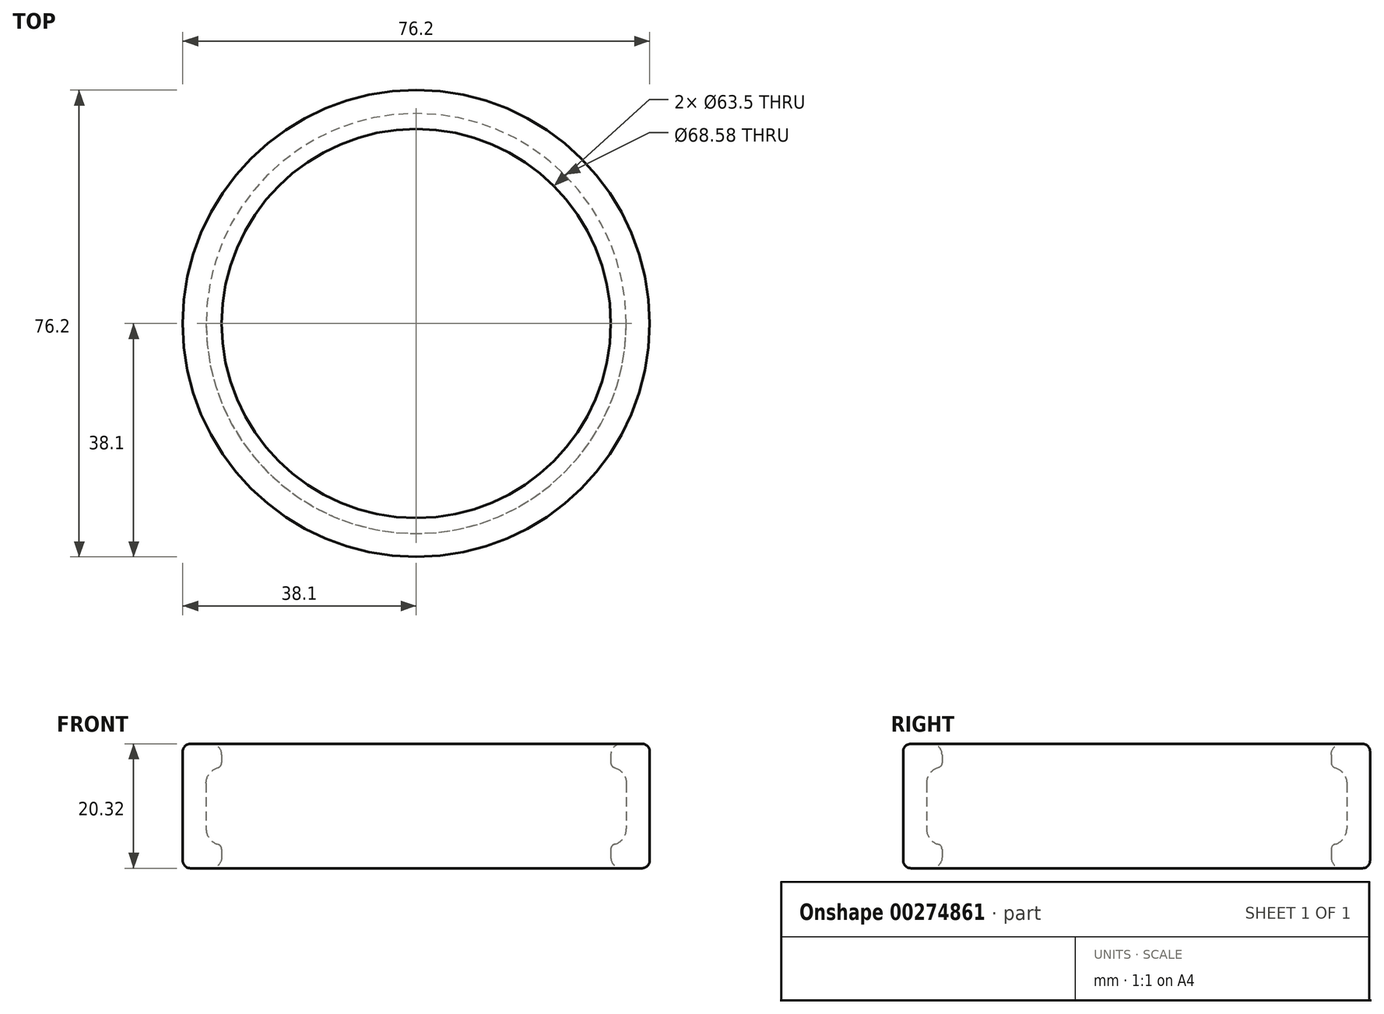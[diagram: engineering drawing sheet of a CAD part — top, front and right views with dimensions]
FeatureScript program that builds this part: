
annotation { "Feature Type Name" : "Feature", "Feature Type Description" : "" }
export const myFeature = defineFeature(function(context is Context, id is Id, definition is map)
    precondition{}
    {
        {
            var Q0;
            Q0=qCreatedBy(makeId("Top.planeOp"),FACE);
            var sketch = newSketch(context, id + "F0", { "sketchPlane" : qUnion([Q0])});
            skCircle(sketch, "E0", {"center": v(0, 0) * mm, "radius": 38.1 * mm});
            skCircle(sketch, "E1", {"center": v(0, 0) * mm, "radius": 31.75 * mm});
            skSolve(sketch);
        }
        {
            var Q0;
            Q0=makeQuery(id+"F0.imprint","IMPRINT",FACE,{"disambiguationData":[TD([[makeQuery(id+"F0.imprint","IMPRINT",EDGE,{"derivedFrom":sQuery(id+"F0.wireOp",EDGE,"E0")}),-1.0]])]});
            var Q1;
            Q1=makeQuery(id+"F0.imprint","IMPRINT",FACE,{"disambiguationData":[TD([[makeQuery(id+"F0.imprint","IMPRINT",EDGE,{"derivedFrom":sQuery(id+"F0.wireOp",EDGE,"E0")}),1.0]])]});
            extrude(context, id + "F1", {"entities" : qUnion([Q0, Q1]), "endBound" : BoundingType.SYMMETRIC, "depth" : 20.32 * mm});
        }
        {
            var Q0;
            Q0=makeQuery(id+"F1.opExtrude","SWEPT_FACE",FACE,{"disambiguationData":[OSD([sQuery(id+"F0.wireOp",EDGE,"E1")])]});
            shell(context, id + "F2", {"entities" : qUnion([Q0]), "thickness" : 3.8 * mm});
        }
        {
            var Q0;
            Q0=makeQuery(id+"F1.opExtrude","CAP_EDGE",EDGE,{"disambiguationData":[OSD([sQuery(id+"F0.wireOp",EDGE,"E1")])],"isStart":false});
            var Q1;
            Q1=makeQuery(id+"F1.opExtrude","CAP_EDGE",EDGE,{"disambiguationData":[OSD([sQuery(id+"F0.wireOp",EDGE,"E1")])],"isStart":true});
            fillet(context, id + "F3", {"entities" : qUnion([Q0, Q1]), "radius" : 1.78 * mm, "tangentPropagation" : true, "allowEdgeOverflow" : false});
        }
        {
            var Q0;
            {var subQ0=sQuery(id+"F0.wireOp",EDGE,"E0");var subQ1=sQuery(id+"F0.wireOp",EDGE,"E1");Q0=makeQuery(id+"FkAHEVNdcQpRxt2_1.opFillet","BLEND_EDGE",EDGE,{"blendedFrom":[makeQuery(id+"F50xpF200IVCPWQ_1.opThicken","CAP_EDGE",EDGE,{"disambiguationData":[OSD([subQ1]),TDD([makeQuery(id+"F2.opShell","OFFSET_EDGE",EDGE,{"disambiguationData":[OSD([subQ1]),TDD([makeQuery(id+"F1.opExtrude","CAP_EDGE",EDGE,{"disambiguationData":[OSD([subQ1])],"isStart":true})])]})])],"isStart":true}),makeQuery(id+"F50xpF200IVCPWQ_1.boolean.opBoolean","MERGE",FACE,{"derivedFrom":[makeQuery(id+"F2.opShell","OFFSET_FACE",FACE,{"disambiguationData":[OSD([subQ0])]}),makeQuery(id+"F50xpF200IVCPWQ_1.opThicken","SWEPT_FACE",FACE,{"disambiguationData":[OSD([subQ0]),TDD([makeQuery(id+"F2.opShell","OFFSET_EDGE",EDGE,{"disambiguationData":[OSD([subQ0]),TDD([makeQuery(id+"F1.opExtrude","CAP_EDGE",EDGE,{"disambiguationData":[OSD([subQ0])],"isStart":true})])]})])]})]})],"blendedInto":[makeQuery(id+"F50xpF200IVCPWQ_1.boolean.opBoolean","MERGE",FACE,{"derivedFrom":[makeQuery(id+"F2.opShell","OFFSET_FACE",FACE,{"disambiguationData":[OSD([subQ0])]}),makeQuery(id+"F50xpF200IVCPWQ_1.opThicken","SWEPT_FACE",FACE,{"disambiguationData":[OSD([subQ0]),TDD([makeQuery(id+"F2.opShell","OFFSET_EDGE",EDGE,{"disambiguationData":[OSD([subQ0]),TDD([makeQuery(id+"F1.opExtrude","CAP_EDGE",EDGE,{"disambiguationData":[OSD([subQ0])],"isStart":true})])]})])]})]})]});}
            var Q1;
            Q1=makeQuery(id+"F1.opExtrude","CAP_EDGE",EDGE,{"disambiguationData":[OSD([sQuery(id+"F0.wireOp",EDGE,"E0")])],"isStart":true});
            var Q2;
            Q2=makeQuery(id+"F1.opExtrude","CAP_EDGE",EDGE,{"disambiguationData":[OSD([sQuery(id+"F0.wireOp",EDGE,"E0")])],"isStart":false});
            var Q3;
            {var subQ0=sQuery(id+"F0.wireOp",EDGE,"E0");var subQ1=sQuery(id+"F0.wireOp",EDGE,"E1");Q3=makeQuery(id+"FkAHEVNdcQpRxt2_1.opFillet","BLEND_EDGE",EDGE,{"blendedFrom":[makeQuery(id+"F50xpF200IVCPWQ_1.opThicken","CAP_EDGE",EDGE,{"disambiguationData":[OSD([subQ1]),TDD([makeQuery(id+"F2.opShell","OFFSET_EDGE",EDGE,{"disambiguationData":[OSD([subQ1]),TDD([makeQuery(id+"F1.opExtrude","CAP_EDGE",EDGE,{"disambiguationData":[OSD([subQ1])],"isStart":false})])]})])],"isStart":true}),makeQuery(id+"F50xpF200IVCPWQ_1.boolean.opBoolean","MERGE",FACE,{"derivedFrom":[makeQuery(id+"F1.opExtrude","SWEPT_FACE",FACE,{"disambiguationData":[OSD([subQ0])]}),makeQuery(id+"F50xpF200IVCPWQ_1.opThicken","SWEPT_FACE",FACE,{"disambiguationData":[OSD([subQ0]),TDD([makeQuery(id+"F2.opShell","OFFSET_EDGE",EDGE,{"disambiguationData":[OSD([subQ0]),TDD([makeQuery(id+"F1.opExtrude","CAP_EDGE",EDGE,{"disambiguationData":[OSD([subQ0])],"isStart":false})])]})])]})]})],"blendedInto":[makeQuery(id+"F50xpF200IVCPWQ_1.boolean.opBoolean","MERGE",FACE,{"derivedFrom":[makeQuery(id+"F1.opExtrude","SWEPT_FACE",FACE,{"disambiguationData":[OSD([subQ0])]}),makeQuery(id+"F50xpF200IVCPWQ_1.opThicken","SWEPT_FACE",FACE,{"disambiguationData":[OSD([subQ0]),TDD([makeQuery(id+"F2.opShell","OFFSET_EDGE",EDGE,{"disambiguationData":[OSD([subQ0]),TDD([makeQuery(id+"F1.opExtrude","CAP_EDGE",EDGE,{"disambiguationData":[OSD([subQ0])],"isStart":false})])]})])]})]})]});}
            fillet(context, id + "F4", {"entities" : qUnion([Q0, Q1, Q2, Q3]), "radius" : 1.27 * mm, "tangentPropagation" : true, "allowEdgeOverflow" : false});
        }
        {
            var Q0;
            {var subQ0=sQuery(id+"F0.wireOp",EDGE,"E0");Q0=makeQuery(id+"F2.opShell","OFFSET_EDGE",EDGE,{"disambiguationData":[OSD([subQ0]),TDD([makeQuery(id+"F1.opExtrude","CAP_EDGE",EDGE,{"disambiguationData":[OSD([subQ0])],"isStart":true})])]});}
            var Q1;
            {var subQ0=sQuery(id+"F0.wireOp",EDGE,"E0");Q1=makeQuery(id+"F2.opShell","OFFSET_EDGE",EDGE,{"disambiguationData":[OSD([subQ0]),TDD([makeQuery(id+"F1.opExtrude","CAP_EDGE",EDGE,{"disambiguationData":[OSD([subQ0])],"isStart":false})])]});}
            fillet(context, id + "F5", {"entities" : qUnion([Q0, Q1]), "radius" : 2.64 * mm, "tangentPropagation" : true, "allowEdgeOverflow" : false});
        }
        {
            var Q0;
            {var subQ0=sQuery(id+"F0.wireOp",EDGE,"E0");Q0=makeQuery(id+"F5.opFillet","BLEND_EDGE",EDGE,{"blendedFrom":[makeQuery(id+"F2.opShell","OFFSET_EDGE",EDGE,{"disambiguationData":[OSD([subQ0]),TDD([makeQuery(id+"F1.opExtrude","CAP_EDGE",EDGE,{"disambiguationData":[OSD([subQ0])],"isStart":true})])]}),makeQuery(id+"F2.opShell","OFFSET_FACE",FACE,{"disambiguationData":[OSD([sQuery(id+"F0.wireOp",EDGE,"E1")])]})],"blendedInto":[makeQuery(id+"F2.opShell","OFFSET_FACE",FACE,{"disambiguationData":[OSD([sQuery(id+"F0.wireOp",EDGE,"E1")])]})]});}
            var Q1;
            {var subQ0=sQuery(id+"F0.wireOp",EDGE,"E0");Q1=makeQuery(id+"F5.opFillet","BLEND_EDGE",EDGE,{"blendedFrom":[makeQuery(id+"F2.opShell","OFFSET_EDGE",EDGE,{"disambiguationData":[OSD([subQ0]),TDD([makeQuery(id+"F1.opExtrude","CAP_EDGE",EDGE,{"disambiguationData":[OSD([subQ0])],"isStart":false})])]}),makeQuery(id+"F1.opExtrude","SWEPT_FACE",FACE,{"disambiguationData":[OSD([sQuery(id+"F0.wireOp",EDGE,"E1")])]})],"blendedInto":[makeQuery(id+"F1.opExtrude","SWEPT_FACE",FACE,{"disambiguationData":[OSD([sQuery(id+"F0.wireOp",EDGE,"E1")])]})]});}
            fillet(context, id + "F6", {"entities" : qUnion([Q0, Q1]), "radius" : 0.85 * mm, "tangentPropagation" : true, "allowEdgeOverflow" : false});
        }
    });
